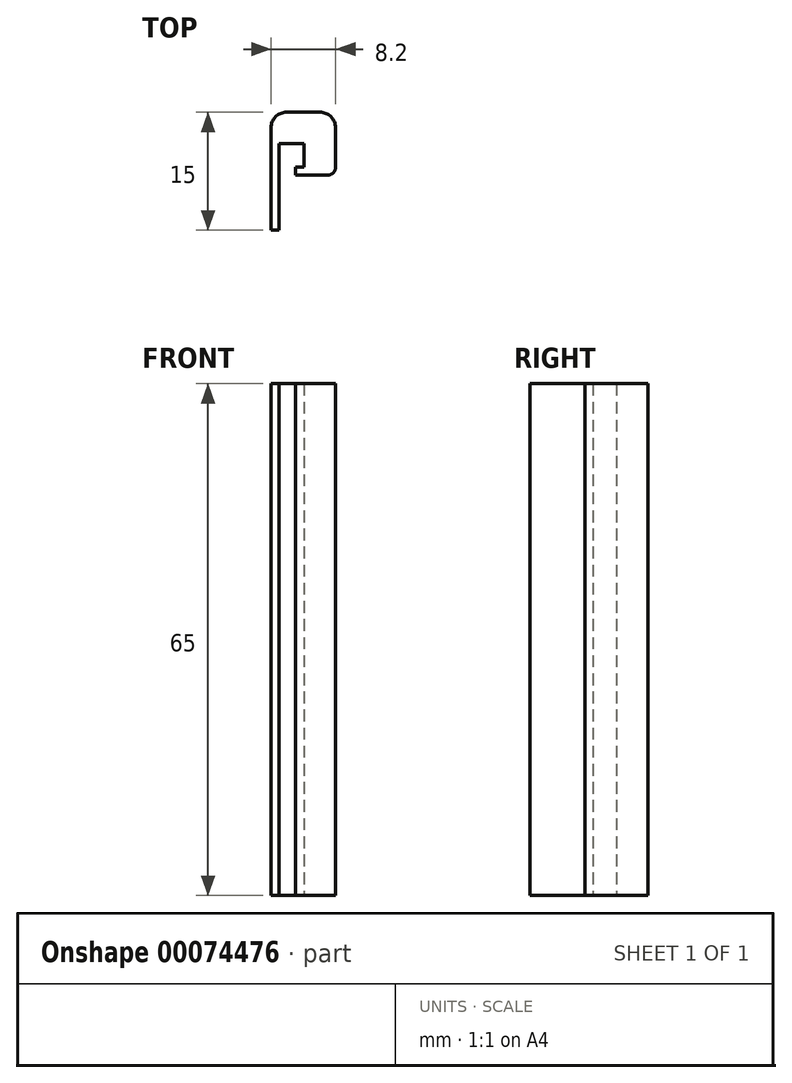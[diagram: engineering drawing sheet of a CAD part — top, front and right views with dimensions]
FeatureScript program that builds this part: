
annotation { "Feature Type Name" : "Feature", "Feature Type Description" : "" }
export const myFeature = defineFeature(function(context is Context, id is Id, definition is map)
    precondition{}
    {
        {
            var Q0;
            Q0=qCreatedBy(makeId("Top.planeOp"),FACE);
            var sketch = newSketch(context, id + "F0", { "sketchPlane" : qUnion([Q0])});
            skLineSegment(sketch, "E0", {"start": v(0, 0) * mm, "end": v(0, 15) * mm});
            skLineSegment(sketch, "E1", {"start": v(0, 15) * mm, "end": v(8.2, 15) * mm});
            skLineSegment(sketch, "E2", {"start": v(8.2, 15) * mm, "end": v(8.2, 7) * mm});
            skLineSegment(sketch, "E3", {"start": v(8.2, 7) * mm, "end": v(4.2, 7) * mm});
            skLineSegment(sketch, "E4", {"start": v(4.2, 8) * mm, "end": v(4.2, 11) * mm});
            skLineSegment(sketch, "E5", {"start": v(4.2, 11) * mm, "end": v(1, 11) * mm});
            skLineSegment(sketch, "E6", {"start": v(1, 11) * mm, "end": v(1, 0) * mm});
            skLineSegment(sketch, "E7", {"start": v(1, 0) * mm, "end": v(0, 0) * mm});
            skLineSegment(sketch, "E8", {"start": v(4.2, 7) * mm, "end": v(3.1, 7) * mm});
            skLineSegment(sketch, "E9", {"start": v(3.1, 7) * mm, "end": v(3.1, 8) * mm});
            skLineSegment(sketch, "E10", {"start": v(3.1, 8) * mm, "end": v(4.2, 8) * mm});
            skSolve(sketch);
        }
        {
            var Q0;
            Q0 = qSketchRegion(id + "F0", true);
            extrude(context, id + "F1", {"entities" : qUnion([Q0]), "depth" : 65 * mm});
        }
        {
            var Q0;
            Q0=makeQuery(id+"F1.opExtrude","SWEPT_EDGE",EDGE,{"disambiguationData":[OSD([sQuery(id+"F0.wireOp",EDGE,"E1"),sQuery(id+"F0.wireOp",EDGE,"E2")])]});
            var Q1;
            Q1=makeQuery(id+"F1.opExtrude","SWEPT_EDGE",EDGE,{"disambiguationData":[OSD([sQuery(id+"F0.wireOp",EDGE,"E0"),sQuery(id+"F0.wireOp",EDGE,"E1")])]});
            fillet(context, id + "F2", {"entities" : qUnion([Q0, Q1]), "radius" : 2 * mm, "tangentPropagation" : true, "allowEdgeOverflow" : false});
        }
        {
            var Q0;
            Q0=makeQuery(id+"F1.opExtrude","SWEPT_EDGE",EDGE,{"disambiguationData":[OSD([sQuery(id+"F0.wireOp",EDGE,"E2"),sQuery(id+"F0.wireOp",EDGE,"E3")])]});
            fillet(context, id + "F3", {"entities" : qUnion([Q0]), "radius" : 1 * mm, "tangentPropagation" : true, "allowEdgeOverflow" : false});
        }
    });
